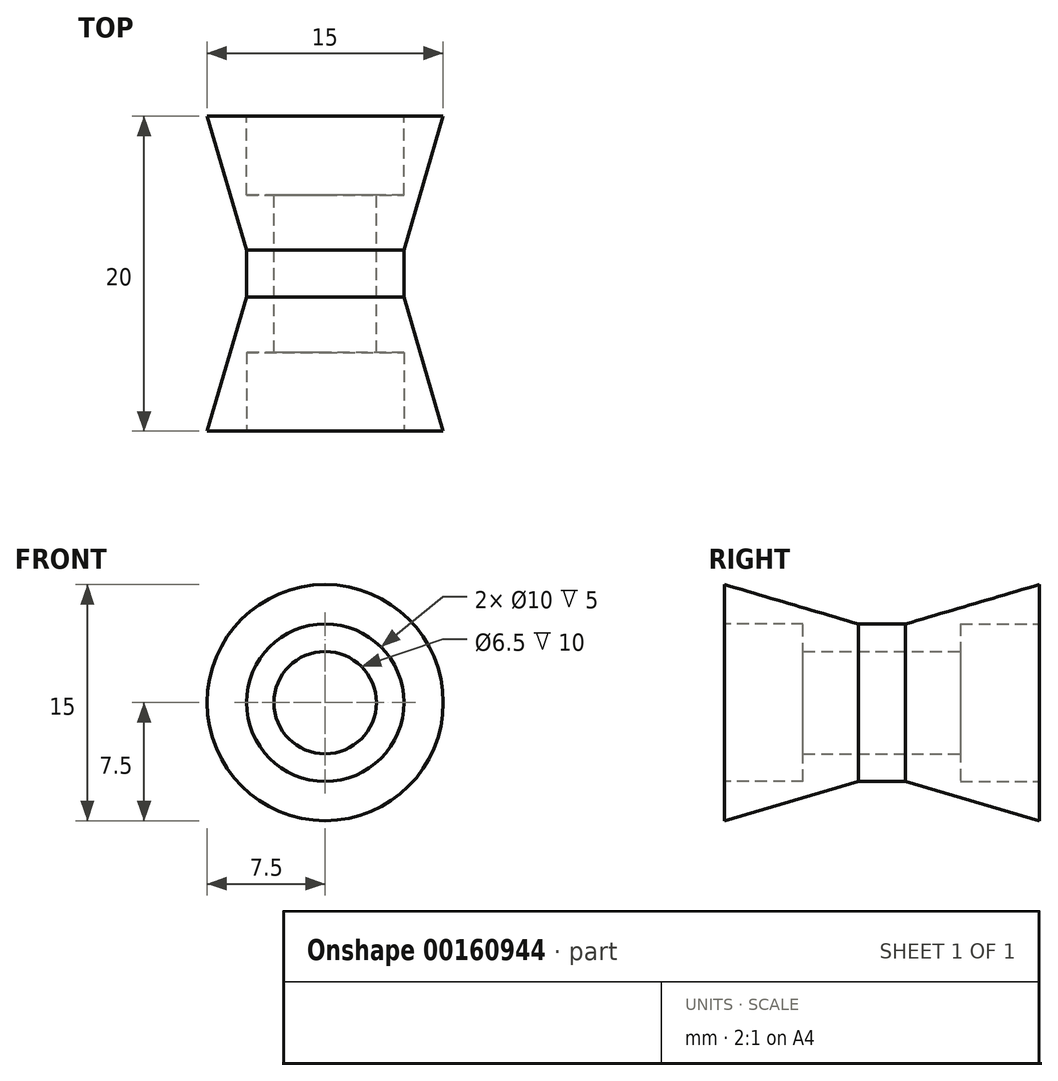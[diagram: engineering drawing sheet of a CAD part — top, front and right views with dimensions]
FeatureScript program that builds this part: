
annotation { "Feature Type Name" : "Feature", "Feature Type Description" : "" }
export const myFeature = defineFeature(function(context is Context, id is Id, definition is map)
    precondition{}
    {
        {
            var Q0;
            Q0=qCreatedBy(makeId("Top.planeOp"),FACE);
            var sketch = newSketch(context, id + "F0", { "sketchPlane" : qUnion([Q0])});
            skLineSegment(sketch, "E0.bottom", {"start": v(7.5, -10) * mm, "end": v(0, -10) * mm});
            skLineSegment(sketch, "E0.top", {"start": v(7.5, 10) * mm, "end": v(0, 10) * mm});
            skPoint(sketch, "E0.middle", {"position": v(0, 0) * mm});
            skLineSegment(sketch, "E1.bottom", {"start": v(5, -1.5) * mm, "end": v(0, -1.5) * mm});
            skLineSegment(sketch, "E1.top", {"start": v(5, 1.5) * mm, "end": v(0, 1.5) * mm});
            skLineSegment(sketch, "E1.left", {"start": v(5, -1.5) * mm, "end": v(5, 1.5) * mm});
            skLineSegment(sketch, "E2", {"start": v(5, 1.5) * mm, "end": v(7.5, 10) * mm});
            skLineSegment(sketch, "E3", {"start": v(5, -1.5) * mm, "end": v(7.5, -10) * mm});
            skLineSegment(sketch, "E4", {"start": v(0, 10) * mm, "end": v(0, -10) * mm});
            skPoint(sketch, "E5.end.orphan", {"position": v(-7.5, -10) * mm});
            skPoint(sketch, "E6.orphan", {"position": v(-7.5, 10) * mm});
            skPoint(sketch, "E1.right.end.orphan", {"position": v(-5, 1.5) * mm});
            skPoint(sketch, "E1.right.start.orphan", {"position": v(-5, -1.5) * mm});
            skSolve(sketch);
        }
        {
            var Q0;
            {var subQ0=sQuery(id+"F0.wireOp",EDGE,"E0.top");Q0=makeQuery(id+"F0.imprint","IMPRINT",FACE,{"disambiguationData":[TD([[makeQuery(id+"F0.imprint","IMPRINT",EDGE,{"derivedFrom":subQ0}),1.0]])]});}
            var Q1;
            {var subQ0=sQuery(id+"F0.wireOp",EDGE,"E0.bottom");Q1=makeQuery(id+"F0.imprint","IMPRINT",FACE,{"disambiguationData":[TD([[makeQuery(id+"F0.imprint","IMPRINT",EDGE,{"derivedFrom":subQ0}),-1.0]])]});}
            var Q2;
            {var subQ0=sQuery(id+"F0.wireOp",EDGE,"E1.bottom");Q2=makeQuery(id+"F0.imprint","IMPRINT",FACE,{"disambiguationData":[TD([[makeQuery(id+"F0.imprint","IMPRINT",EDGE,{"derivedFrom":subQ0}),-1.0]])]});}
            var Q3;
            Q3=sQuery(id+"F0.wireOp",EDGE,"E4");
            revolve(context, id + "F1", {"entities" : qUnion([Q0, Q1, Q2]), "axis" : qUnion([Q3]), "revolveType" : RevolveType.FULL});
        }
        {
            var Q0;
            Q0=makeQuery(id+"F1.opRevolve","SWEPT_FACE",FACE,{"disambiguationData":[OSD([sQuery(id+"F0.wireOp",EDGE,"E0.top")])]});
            var sketch = newSketch(context, id + "F2", { "sketchPlane" : qUnion([Q0])});
            skPoint(sketch, "E7", {"position": v(0, 0) * mm});
            skSolve(sketch);
        }
        {
            var Q0;
            Q0=sQuery(id+"F2.wireOp",VERTEX,"E7");
            var Q1;
            Q1=makeQuery(id+"F1.opRevolve","SWEPT_BODY",BODY,{"disambiguationData":[OSD([sQuery(id+"F0.wireOp",EDGE,"E0.bottom"),sQuery(id+"F0.wireOp",EDGE,"E0.top"),sQuery(id+"F0.wireOp",EDGE,"E1.left"),sQuery(id+"F0.wireOp",EDGE,"E2"),sQuery(id+"F0.wireOp",EDGE,"E3"),sQuery(id+"F0.wireOp",EDGE,"E4")])]});
            hole(context, id + "F3", {"style" : HoleStyle.C_BORE, "endStyle" : HoleEndStyle.THROUGH, "holeDiameter" : 6.5 * mm, "cBoreDiameter" : 10 * mm, "cBoreDepth" : 5 * mm, "locations" : qUnion([Q0]), "scope" : qUnion([Q1]), "isTappedThrough" : true});
        }
        {
            var Q0;
            Q0=makeQuery(id+"F1.opRevolve","SWEPT_FACE",FACE,{"disambiguationData":[OSD([sQuery(id+"F0.wireOp",EDGE,"E0.bottom")])]});
            var sketch = newSketch(context, id + "F4", { "sketchPlane" : qUnion([Q0])});
            skPoint(sketch, "E8", {"position": v(0, 0) * mm});
            skCircle(sketch, "E9", {"center": v(0, 0) * mm, "radius": 5 * mm});
            skSolve(sketch);
        }
        {
            var Q0;
            Q0=makeQuery(id+"F4.imprint","IMPRINT",FACE,{"disambiguationData":[TD([[makeQuery(id+"F4.imprint","IMPRINT",EDGE,{"derivedFrom":sQuery(id+"F4.wireOp",EDGE,"E9")}),1.0]])]});
            extrude(context, id + "F5", {"entities" : qUnion([Q0]), "operationType" : NewBodyOperationType.REMOVE, "oppositeDirection" : true, "depth" : 5 * mm});
        }
    });
